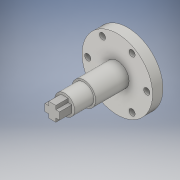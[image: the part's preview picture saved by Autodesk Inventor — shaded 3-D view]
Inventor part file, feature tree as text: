
AUTODESK INVENTOR PART (.ipt)
format: ipt  version: 2016 (Build 200138000, 138)  size: 219,648 bytes
history: native  units: in
note: dims shown in document units (in); Inventor stores cm internally (conversion verified against a paired STEP export)
features: extrude x7, sketch x7, thread x1
ambient origin geometry x8: Origin, YZ Plane, XZ Plane, XY Plane, X Axis, Y Axis, Z Axis, Center Point
bodies: Solid1 (feature_tree)
feature tree (15):
  extrude  "Extrusion1"  Depth=0.3307in TaperAngle=0.0deg
  extrude  "Extrusion2"  Depth=0.939in
  extrude  "Extrusion3"  Depth=0.939in
  extrude  "Extrusion4"  Depth=0.939in
  extrude  "Extrusion6"  Depth=0.939in
  extrude  "Extrusion7"  Depth=0.939in
  thread  "Thread3"  [1 undecoded]
  extrude  "Extrusion11"  Depth=0.1969in
  sketch  "Sketch1"  dims[d0=2.2402in d1=0.3307in d2=0.0in]
  sketch  "Sketch2"  dims[d3=0.939in d4=0.939in]
  sketch  "Sketch3"  dims[d5=60.0deg d6=0.939in]
  sketch  "Sketch4"  dims[d7=120.0deg d8=0.939in]
  sketch  "Sketch6"  dims[d9=180.0deg d10=0.939in]
  sketch  "Sketch7"  dims[d11=60.0deg d12=0.939in d13=120.0deg]
  sketch  "Sketch12"  dims[d14=0.1969in d15=0.1969in d16=0.1969in d17=0.1969in d18=0.1969in d19=0.1969in d20=0.3307in d21=0.0in d22=0.748in d23=1.063in d24=0.0in d25=0.6299in d26=0.6102in d27=0.0in d89=0.2362in d90=0.0in d91=0.1181in d92=0.1969in d93=0.0in d103=0.3937in d104=0.0in d120=0.3543in d121=0.0787in d122=0.2756in d124=0.2756in d125=0.1575in d126=0.2756in d127=0.2756in d128=0.1575in d129=0.2756in d130=0.2756in d131=0.1575in d132=0.2756in d133=0.2756in d221=0.2323in d222=0.1142in d223=0.1142in d224=0.1181in d225=0.1181in d226=0.1181in d227=0.1181in d228=0.2283in d229=0.1181in d230=0.1181in d231=0.2283in d232=0.1181in d233=0.1181in d234=0.3937in d235=0.0in]
note: 1 required parameter value undecoded (feature->parameter linkage not recoverable at this tier; creation-order binding heuristic only, values carry confidence <= 0.55)
